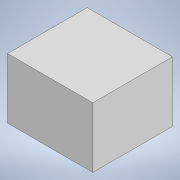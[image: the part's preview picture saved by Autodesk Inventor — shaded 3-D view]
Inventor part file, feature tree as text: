
AUTODESK INVENTOR PART (.ipt)
format: ipt  version: 2021 (Build 250183000, 183)  size: 202,240 bytes
history: native  units: mm
features: extrude x4, sketch x4, projected_geometry x2
ambient origin geometry x8: Origin, YZ Plane, XZ Plane, XY Plane, X Axis, Y Axis, Z Axis, Center Point
bodies: Solid2 (feature_tree), Solid1 (feature_tree)
feature tree (10):
  extrude  "Extrusion1"  Depth=3.0mm TaperAngle=0.0deg
  extrude  "Extrusion2"  Depth=3.0mm TaperAngle=0.0deg
  extrude  "Extrusion3"  [1 undecoded]
  extrude  "Extrusion4"  [1 undecoded]
  sketch  "Sketch1"  dims[d0=3.0mm d1=0.0mm d3=3.0mm d4=0.0mm]
  projected_geometry  "Projected Loop1"
  sketch  "Sketch2"  dims[d5=30.0mm d6=0.0mm d7=3.0mm d8=0.0mm]
  projected_geometry  "Projected Loop2"
  sketch  "Sketch3"
  sketch  "Sketch4"
note: 2 required parameter values undecoded (feature->parameter linkage not recoverable at this tier; creation-order binding heuristic only, values carry confidence <= 0.55)
